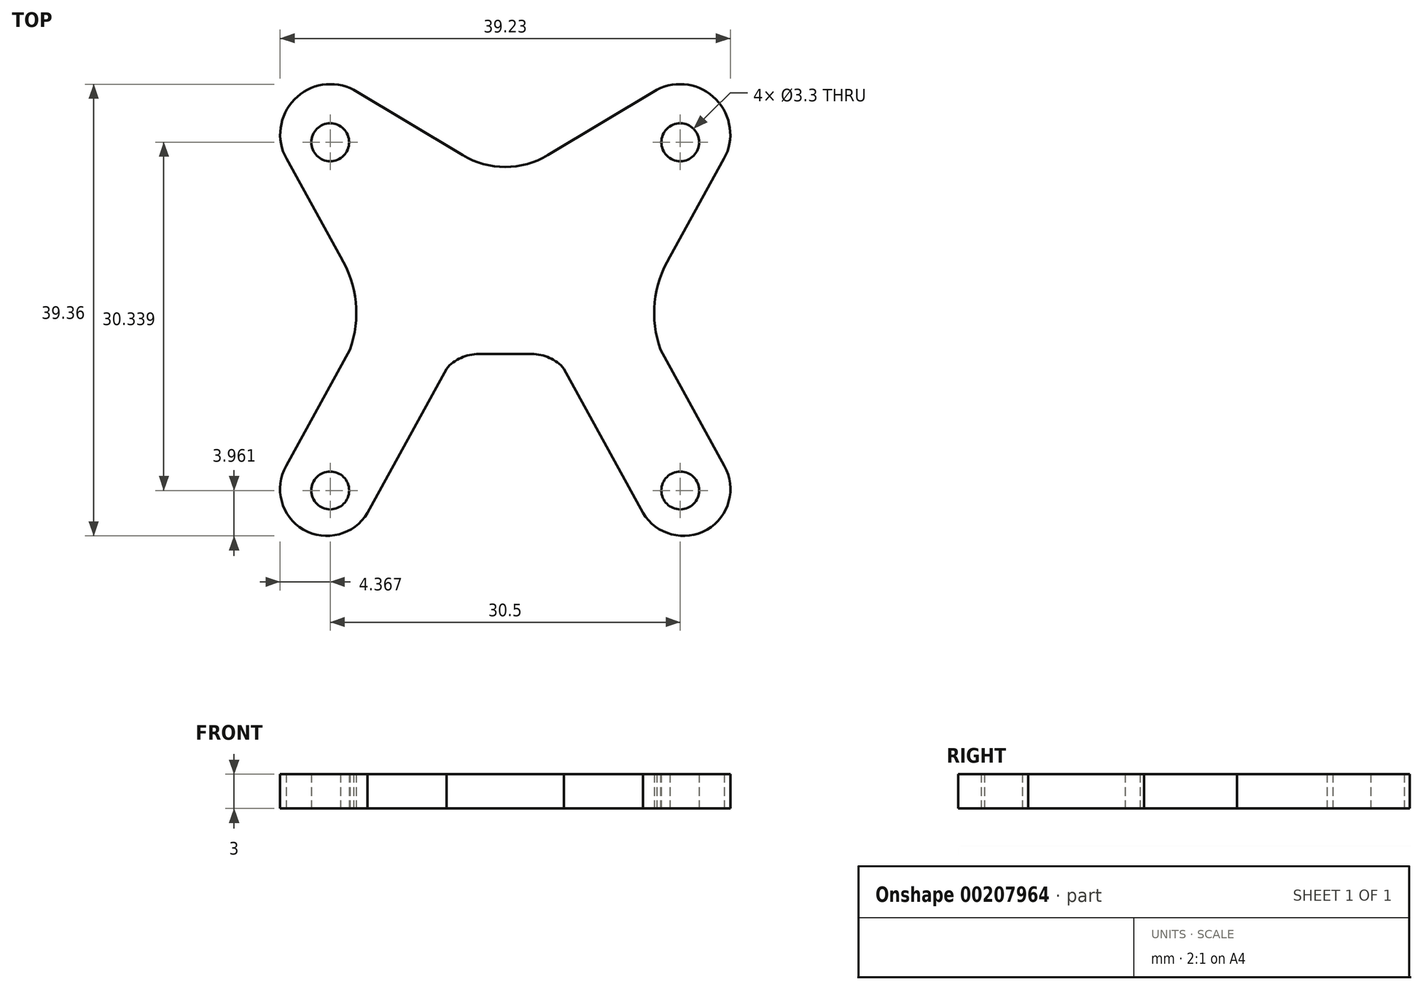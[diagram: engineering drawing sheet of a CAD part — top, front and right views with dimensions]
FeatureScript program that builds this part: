
annotation { "Feature Type Name" : "Feature", "Feature Type Description" : "" }
export const myFeature = defineFeature(function(context is Context, id is Id, definition is map)
    precondition{}
    {
        {
            var Q0;
            Q0=qCreatedBy(makeId("Top.planeOp"),FACE);
            var sketch = newSketch(context, id + "F0", { "sketchPlane" : qUnion([Q0])});
            skLineSegment(sketch, "E0", {"start": v(-2.8, 33.8) * mm, "end": v(27.7, 33.8) * mm, "construction": true});
            skLineSegment(sketch, "E1", {"start": v(-2.8, 33.8) * mm, "end": v(-2.8, 3.45) * mm, "construction": true});
            skLineSegment(sketch, "E2", {"start": v(-2.8, 3.45) * mm, "end": v(27.7, 3.45) * mm, "construction": true});
            skLineSegment(sketch, "E3", {"start": v(27.7, 33.8) * mm, "end": v(27.7, 3.45) * mm, "construction": true});
            skCircle(sketch, "E4", {"center": v(27.7, 3.45) * mm, "radius": 1.65 * mm});
            skCircle(sketch, "E5.1.0.0", {"center": v(-2.8, 3.45) * mm, "radius": 1.65 * mm});
            skLineSegment(sketch, "E5.direction1", {"start": v(27.7, 3.45) * mm, "end": v(-2.8, 3.45) * mm, "construction": true});
            skLineSegment(sketch, "E6", {"start": v(-2.8, 18.62) * mm, "end": v(27.7, 18.62) * mm, "construction": true});
            skCircle(sketch, "E7.MirrorC", {"center": v(-2.8, 33.8) * mm, "radius": 1.65 * mm});
            skCircle(sketch, "E8.MirrorC", {"center": v(27.7, 33.8) * mm, "radius": 1.65 * mm});
            skLineSegment(sketch, "E9", {"start": v(16.18, 32.66) * mm, "end": v(25.67, 38.37) * mm});
            skLineSegment(sketch, "E10", {"start": v(31.52, 32.35) * mm, "end": v(26.8, 23.8) * mm});
            skArc(sketch, "E11", {"start": v(31.52, 32.35) * mm, "mid": v(30.82, 37.53) * mm, "end": v(25.67, 38.37) * mm});
            skPoint(sketch, "E12.center", {"position": v(12.46, 18.62) * mm});
            skLineSegment(sketch, "E13", {"start": v(12.46, 33.8) * mm, "end": v(12.46, 3.45) * mm, "construction": true});
            skLineSegment(sketch, "E14.MirrorCS", {"start": v(8.74, 32.66) * mm, "end": v(-0.75, 38.37) * mm});
            skArc(sketch, "E15.MirrorCS", {"start": v(-6.6, 32.35) * mm, "mid": v(-5.9, 37.53) * mm, "end": v(-0.75, 38.37) * mm});
            skLineSegment(sketch, "E16.MirrorCS", {"start": v(-6.6, 32.35) * mm, "end": v(-1.9, 23.8) * mm});
            skArc(sketch, "E17", {"start": v(8.74, 32.66) * mm, "mid": v(12.46, 31.63) * mm, "end": v(16.18, 32.66) * mm});
            skLineSegment(sketch, "E18", {"start": v(10.16, 15.34) * mm, "end": v(12.46, 15.34) * mm});
            skLineSegment(sketch, "E19", {"start": v(26, 15.71) * mm, "end": v(31.54, 5.6) * mm});
            skLineSegment(sketch, "E20", {"start": v(17.58, 14.05) * mm, "end": v(24.47, 1.5) * mm});
            skArc(sketch, "E21", {"start": v(24.47, 1.5) * mm, "mid": v(30.03, 0.04) * mm, "end": v(31.54, 5.6) * mm});
            skLineSegment(sketch, "E22.MirrorCS", {"start": v(12.46, -3.1) * mm, "end": v(12.46, 27.24) * mm, "construction": true});
            skLineSegment(sketch, "E23.MirrorCS", {"start": v(14.76, 15.34) * mm, "end": v(12.46, 15.34) * mm});
            skArc(sketch, "E24", {"start": v(17.58, 14.05) * mm, "mid": v(16.3, 15) * mm, "end": v(14.76, 15.34) * mm});
            skArc(sketch, "E25", {"start": v(26.8, 23.8) * mm, "mid": v(25.48, 19.85) * mm, "end": v(26, 15.71) * mm});
            skArc(sketch, "E26.MirrorCS", {"start": v(-1.9, 23.8) * mm, "mid": v(-0.57, 19.85) * mm, "end": v(-1.08, 15.71) * mm});
            skLineSegment(sketch, "E27.MirrorCS", {"start": v(-1.08, 15.71) * mm, "end": v(-6.63, 5.6) * mm});
            skArc(sketch, "E28.MirrorCS", {"start": v(0.45, 1.5) * mm, "mid": v(-5.12, 0.04) * mm, "end": v(-6.63, 5.6) * mm});
            skLineSegment(sketch, "E29.MirrorCS", {"start": v(7.33, 14.05) * mm, "end": v(0.45, 1.5) * mm});
            skArc(sketch, "E30.MirrorCS", {"start": v(7.33, 14.05) * mm, "mid": v(8.6, 15) * mm, "end": v(10.16, 15.34) * mm});
            skSolve(sketch);
        }
        {
            var Q0;
            Q0 = qSketchRegion(id + "F0", true);
            var Q1;
            Q1=makeQuery(id+"F0.imprint","IMPRINT",FACE,{"disambiguationData":[TD([[makeQuery(id+"F0.imprint","IMPRINT",EDGE,{"derivedFrom":sQuery(id+"F0.wireOp",EDGE,"E4")}),-1.0]])]});
            extrude(context, id + "F1", {"entities" : qUnion([Q0, Q1]), "depth" : 3 * mm});
        }
    });
